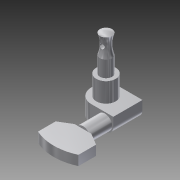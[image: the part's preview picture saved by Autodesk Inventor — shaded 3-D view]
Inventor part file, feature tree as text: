
AUTODESK INVENTOR PART (.ipt)
format: ipt  version: 2013 (Build 170138000, 138)  size: 196,096 bytes
history: native  units: mm
features: sketch x8, extrude x7, projected_geometry x2, revolve x1, fillet x1
ambient origin geometry x8: Origin, YZ Plane, XZ Plane, XY Plane, X Axis, Y Axis, Z Axis, Center Point
bodies: Solid1 (feature_tree)
feature tree (19):
  extrude  "Extrusion1"  Depth=11.43mm
  extrude  "Extrusion2"  Depth=10.16mm
  revolve  "Revolution1"  [1 undecoded]
  extrude  "Extrusion3"  Depth=2.286mm
  extrude  "Extrusion4"  Depth=0.635mm
  fillet  "Fillet1"  [1 undecoded]
  extrude  "Extrusion5"  Depth=0.4mm TaperAngle=0.0deg
  extrude  "Extrusion6"  Depth=3.175mm
  extrude  "Extrusion7"  Depth=5.715mm
  sketch  "Sketch1"  dims[d0=15.24mm d2=11.43mm]
  sketch  "Sketch2"  dims[d3=8.89mm d4=0.0mm d5=10.16mm]
  sketch  "Sketch3"  dims[d8=10.16mm d9=0.0mm d10=3.175mm]
  sketch  "Sketch4"  dims[d13=8.382mm d14=2.286mm]
  sketch  "Sketch5"  dims[d15=19.05mm d16=0.635mm d17=90.0deg]
  sketch  "Sketch6"  dims[d18=2.54mm d21=0.4mm d22=0.0mm]
  sketch  "Sketch7"  dims[d23=2.25mm d25=3.175mm]
  sketch  "Sketch8"  dims[d26=8.001mm d27=5.715mm d29=2.159mm d30=0.0mm d31=135.0deg d32=4.4mm d33=7.62mm d35=11.43mm d36=0.0mm d37=21.082mm d40=5.08mm d41=15.24mm d42=0.0mm d43=15.24mm d44=0.0mm]
  projected_geometry  "Project Cut Edges1"
  projected_geometry  "Project Cut Edges2"
note: 2 required parameter values undecoded (feature->parameter linkage not recoverable at this tier; creation-order binding heuristic only, values carry confidence <= 0.55)